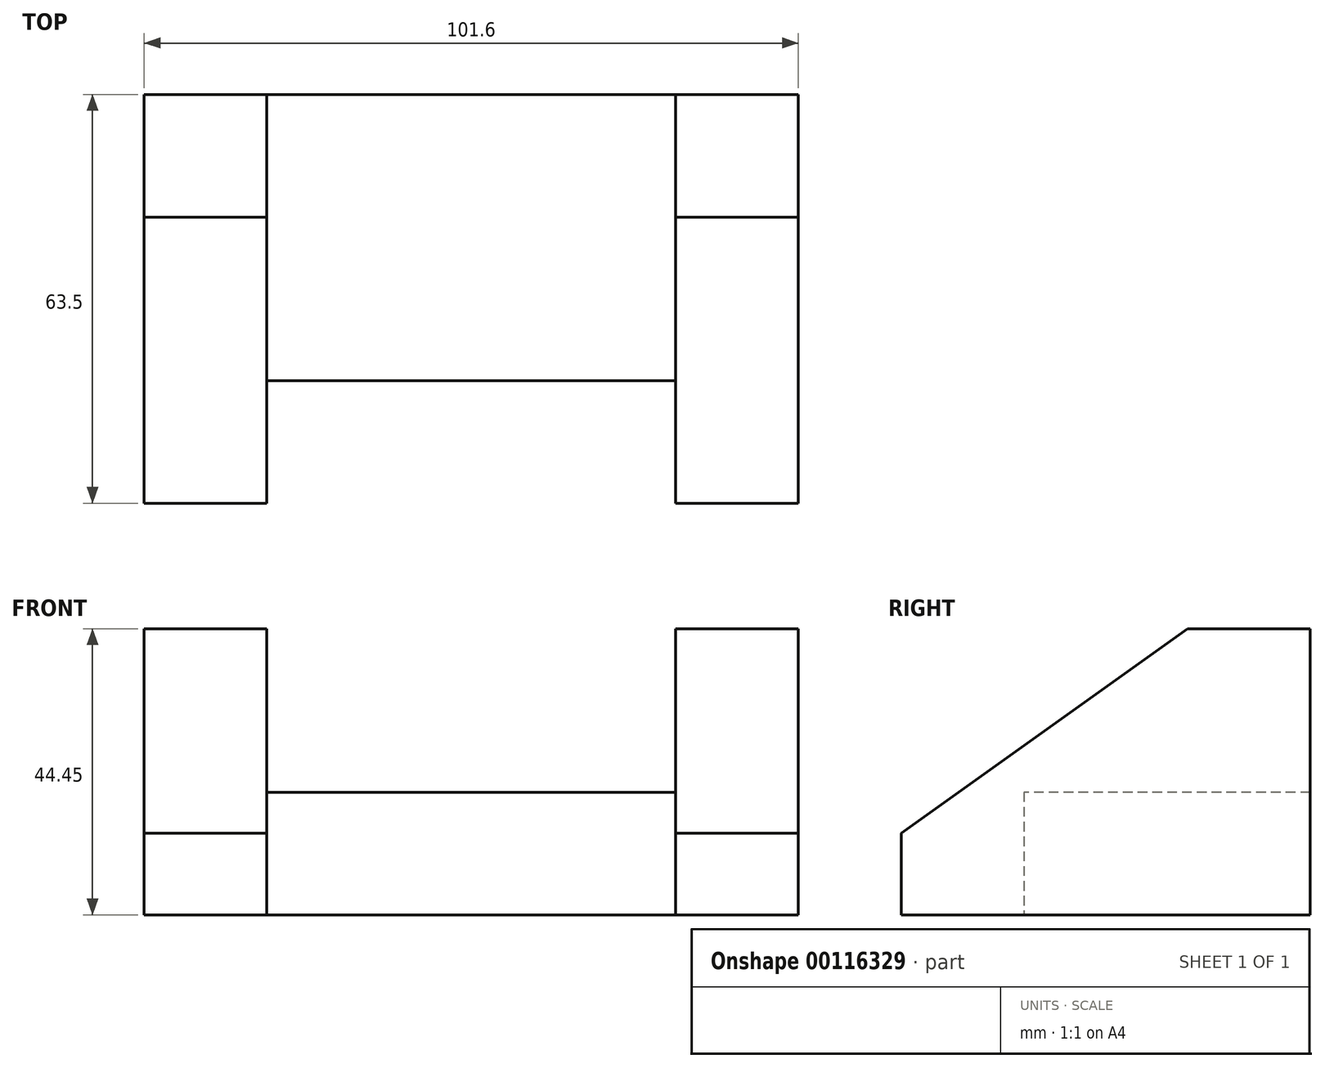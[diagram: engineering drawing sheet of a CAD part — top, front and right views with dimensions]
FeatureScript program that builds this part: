
annotation { "Feature Type Name" : "Feature", "Feature Type Description" : "" }
export const myFeature = defineFeature(function(context is Context, id is Id, definition is map)
    precondition{}
    {
        {
            var Q0;
            Q0=qCreatedBy(makeId("Top.planeOp"),FACE);
            var sketch = newSketch(context, id + "F0", { "sketchPlane" : qUnion([Q0])});
            skLineSegment(sketch, "E0.bottom", {"start": v(-32.48, 0) * mm, "end": v(-0.73, 0) * mm});
            skLineSegment(sketch, "E0.top", {"start": v(-32.48, -44.45) * mm, "end": v(-0.73, -44.45) * mm});
            skLineSegment(sketch, "E0.left", {"start": v(-32.48, 0) * mm, "end": v(-32.48, -44.45) * mm});
            skLineSegment(sketch, "E0.right", {"start": v(-0.73, 0) * mm, "end": v(-0.73, -44.45) * mm});
            skSolve(sketch);
        }
        {
            var Q0;
            Q0 = qSketchRegion(id + "F0", true);
            extrude(context, id + "F1", {"entities" : qUnion([Q0]), "depth" : 19.05 * mm});
        }
        {
            var Q0;
            Q0=makeQuery(id+"F1.opExtrude","SWEPT_FACE",FACE,{"disambiguationData":[OSD([sQuery(id+"F0.wireOp",EDGE,"E0.right")])]});
            var sketch = newSketch(context, id + "F2", { "sketchPlane" : qUnion([Q0])});
            skLineSegment(sketch, "E1", {"start": v(-63.5, 0) * mm, "end": v(-63.5, 12.7) * mm});
            skLineSegment(sketch, "E2", {"start": v(-63.5, 12.7) * mm, "end": v(-19.05, 44.45) * mm});
            skLineSegment(sketch, "E3", {"start": v(-19.05, 44.45) * mm, "end": v(0, 44.45) * mm});
            skLineSegment(sketch, "E4", {"start": v(0, 44.45) * mm, "end": v(0, 0) * mm});
            skLineSegment(sketch, "E5", {"start": v(0, 0) * mm, "end": v(-63.5, 0) * mm});
            skSolve(sketch);
        }
        {
            var Q0;
            Q0 = qSketchRegion(id + "F2", true);
            extrude(context, id + "F3", {"entities" : qUnion([Q0]), "operationType" : NewBodyOperationType.ADD, "depth" : 19.05 * mm});
        }
        {
            var Q0;
            Q0=makeQuery(id+"F1.opExtrude","SWEPT_BODY",BODY,{"disambiguationData":[OSD([sQuery(id+"F0.wireOp",EDGE,"E0.bottom"),sQuery(id+"F0.wireOp",EDGE,"E0.top"),sQuery(id+"F0.wireOp",EDGE,"E0.left"),sQuery(id+"F0.wireOp",EDGE,"E0.right")])]});
            var Q1;
            Q1=makeQuery(id+"F1.opExtrude","SWEPT_FACE",FACE,{"disambiguationData":[OSD([sQuery(id+"F0.wireOp",EDGE,"E0.left")])]});
            mirror(context, id + "F4", {"operationType" : NewBodyOperationType.ADD, "entities" : qUnion([Q0]), "mirrorPlane" : qUnion([Q1])});
        }
    });
